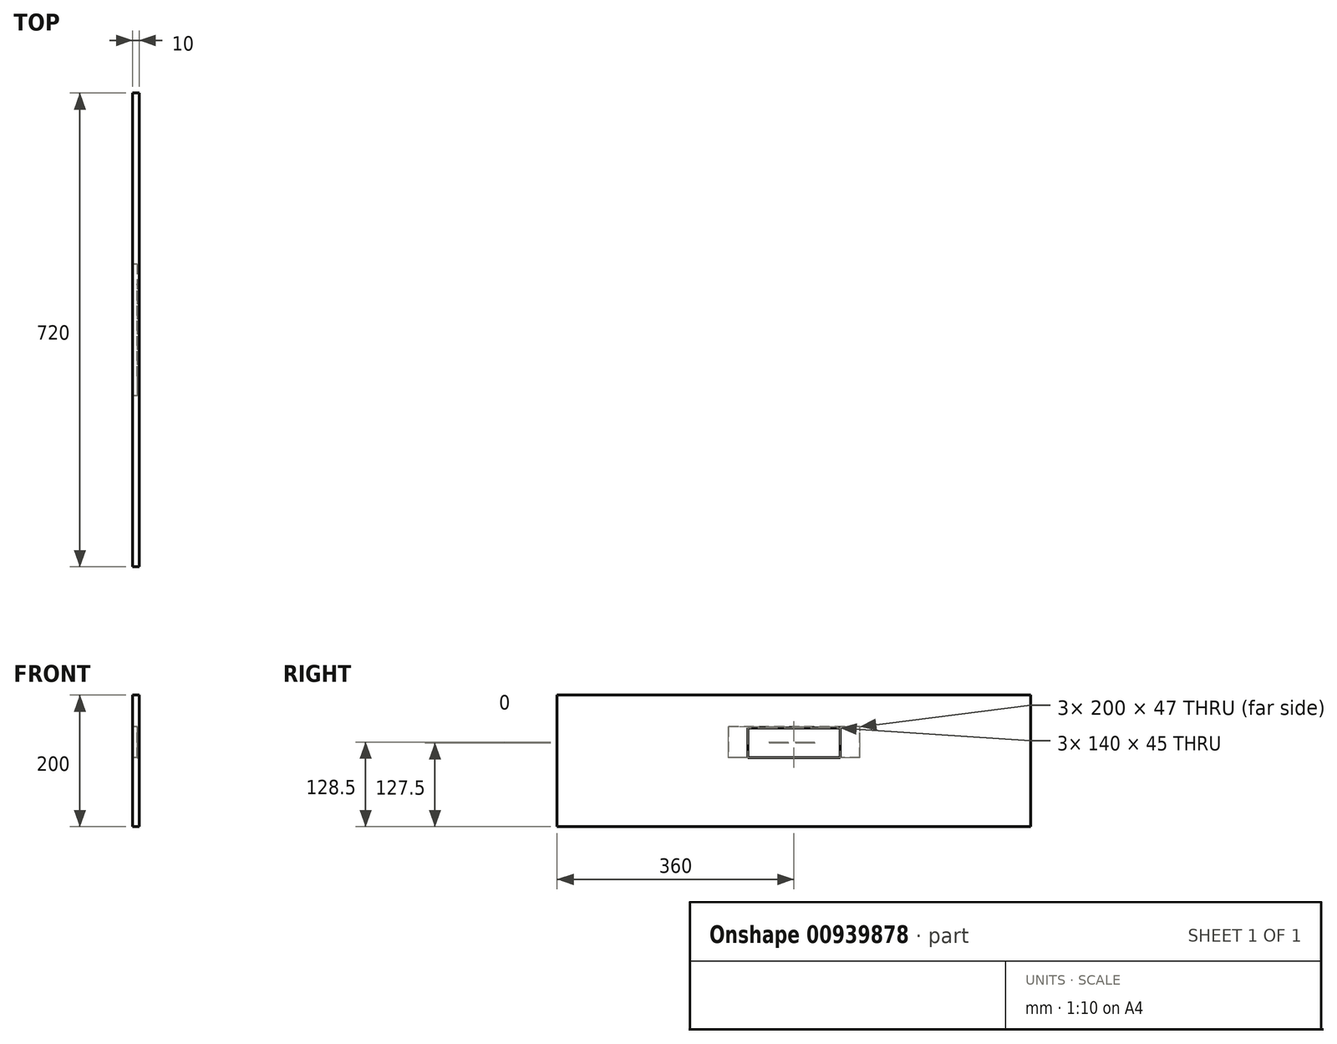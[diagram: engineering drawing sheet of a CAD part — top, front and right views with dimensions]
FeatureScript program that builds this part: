
annotation { "Feature Type Name" : "Feature", "Feature Type Description" : "" }
export const myFeature = defineFeature(function(context is Context, id is Id, definition is map)
    precondition{}
    {
        {
            var Q0;
            Q0=qCreatedBy(makeId("Right.planeOp"),FACE);
            var sketch = newSketch(context, id + "F0", { "sketchPlane" : qUnion([Q0])});
            skLineSegment(sketch, "E0.bottom", {"start": v(-360, 100) * mm, "end": v(360, 100) * mm});
            skLineSegment(sketch, "E0.top", {"start": v(-360, -100) * mm, "end": v(360, -100) * mm});
            skLineSegment(sketch, "E0.left", {"start": v(-360, 100) * mm, "end": v(-360, -100) * mm});
            skLineSegment(sketch, "E0.right", {"start": v(360, 100) * mm, "end": v(360, -100) * mm});
            skPoint(sketch, "E0.middle", {"position": v(0, 0) * mm});
            skSolve(sketch);
        }
        {
            var Q0;
            Q0 = qSketchRegion(id + "F0", true);
            extrude(context, id + "F1", {"entities" : qUnion([Q0]), "depth" : 10 * mm, "offsetDistance" : 25 * mm});
        }
        {
            var Q0;
            Q0=makeQuery(id+"F1.opExtrude","CAP_FACE",FACE,{"disambiguationData":[OSD([sQuery(id+"F0.wireOp",EDGE,"E0.bottom"),sQuery(id+"F0.wireOp",EDGE,"E0.top"),sQuery(id+"F0.wireOp",EDGE,"E0.left"),sQuery(id+"F0.wireOp",EDGE,"E0.right")])],"isStart":false});
            var sketch = newSketch(context, id + "F2", { "sketchPlane" : qUnion([Q0])});
            skLineSegment(sketch, "E1", {"start": v(0, 5) * mm, "end": v(-70, 5) * mm});
            skLineSegment(sketch, "E2", {"start": v(-70, 5) * mm, "end": v(-70, 50) * mm});
            skLineSegment(sketch, "E3", {"start": v(-70, 50) * mm, "end": v(70, 50) * mm});
            skLineSegment(sketch, "E4", {"start": v(70, 50) * mm, "end": v(70, 5) * mm});
            skLineSegment(sketch, "E5", {"start": v(70, 5) * mm, "end": v(0, 5) * mm});
            skSolve(sketch);
        }
        {
            var Q0;
            Q0 = qSketchRegion(id + "F2", true);
            extrude(context, id + "F3", {"entities" : qUnion([Q0]), "operationType" : NewBodyOperationType.REMOVE, "oppositeDirection" : true, "depth" : 25 * mm, "offsetDistance" : 25 * mm});
        }
        {
            var Q0;
            Q0=makeQuery(id+"F1.opExtrude","CAP_FACE",FACE,{"disambiguationData":[OSD([sQuery(id+"F0.wireOp",EDGE,"E0.bottom"),sQuery(id+"F0.wireOp",EDGE,"E0.top"),sQuery(id+"F0.wireOp",EDGE,"E0.left"),sQuery(id+"F0.wireOp",EDGE,"E0.right")])],"isStart":true});
            var sketch = newSketch(context, id + "F4", { "sketchPlane" : qUnion([Q0])});
            skLineSegment(sketch, "E6", {"start": v(0, 5) * mm, "end": v(-100, 5) * mm});
            skLineSegment(sketch, "E7", {"start": v(-100, 5) * mm, "end": v(-100, 52) * mm});
            skLineSegment(sketch, "E8", {"start": v(-100, 52) * mm, "end": v(100, 52) * mm});
            skLineSegment(sketch, "E9", {"start": v(100, 52) * mm, "end": v(100, 5) * mm});
            skLineSegment(sketch, "E10", {"start": v(100, 5) * mm, "end": v(0, 5) * mm});
            skSolve(sketch);
        }
        {
            var Q0;
            Q0 = qSketchRegion(id + "F4", true);
            extrude(context, id + "F5", {"entities" : qUnion([Q0]), "operationType" : NewBodyOperationType.REMOVE, "oppositeDirection" : true, "depth" : 7 * mm, "offsetDistance" : 25 * mm});
        }
    });
